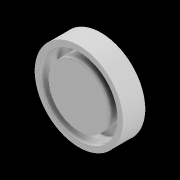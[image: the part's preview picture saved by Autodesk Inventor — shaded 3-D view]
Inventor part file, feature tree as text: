
AUTODESK INVENTOR PART (.ipt)
format: ipt  version: 2020 (Build 240168000, 168)  size: 142,848 bytes
history: native  units: mm
features: extrude x5, sketch x5, fillet x2, other x1, projected_geometry x1
ambient origin geometry x8: Origin, YZ Plane, XZ Plane, XY Plane, X Axis, Y Axis, Z Axis, Center Point
bodies: Body1 (feature_tree)
feature tree (14):
  other  "實體1"
  extrude  "擠出1"  Depth=160.0mm
  extrude  "擠出2"  Depth=140.0mm
  extrude  "擠出3"  Depth=110.0mm
  extrude  "擠出4"  Depth=30.0mm TaperAngle=0.0deg
  fillet  "圓角1"  Radius=10.0mm
  fillet  "圓角2"  Radius=50.0mm
  extrude  "擠出5"  Depth=5.0mm TaperAngle=0.0deg
  sketch  "草圖1"
  sketch  "草圖2"
  sketch  "草圖3"
  sketch  "草圖4"
  projected_geometry  "投影迴路1"
  sketch  "草圖5"
